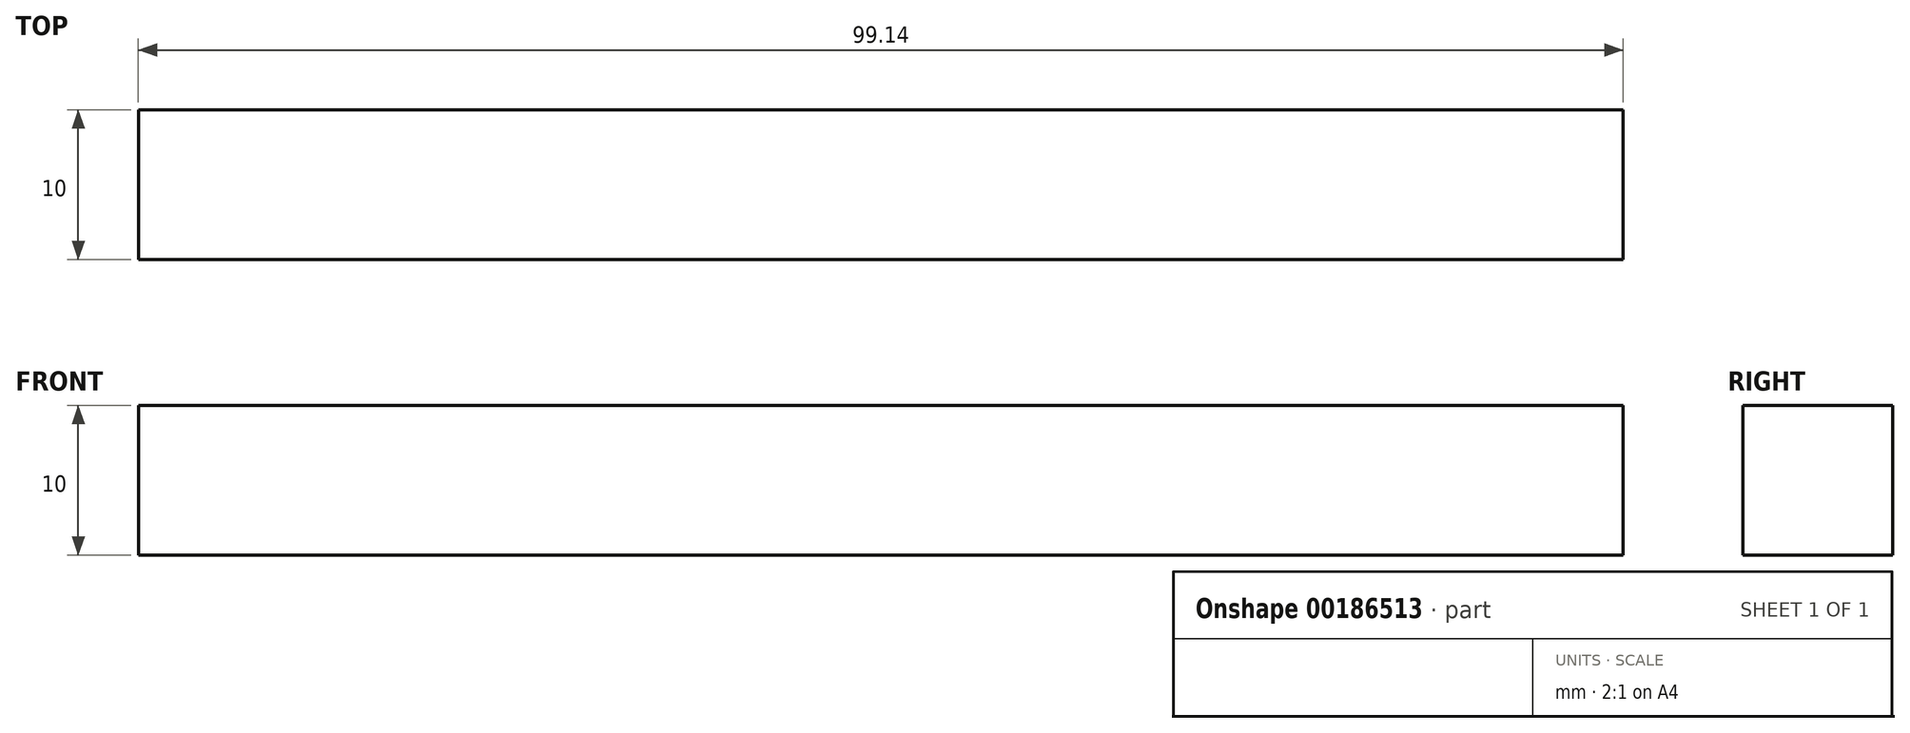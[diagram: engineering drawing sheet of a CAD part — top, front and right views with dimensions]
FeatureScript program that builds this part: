
annotation { "Feature Type Name" : "Feature", "Feature Type Description" : "" }
export const myFeature = defineFeature(function(context is Context, id is Id, definition is map)
    precondition{}
    {
        {
            var Q0;
            Q0=qCreatedBy(makeId("Front.planeOp"),FACE);
            var sketch = newSketch(context, id + "F0", { "sketchPlane" : qUnion([Q0])});
            skLineSegment(sketch, "E0.bottom", {"start": v(-42.53, -4.81) * mm, "end": v(56.6, -4.81) * mm});
            skLineSegment(sketch, "E0.top", {"start": v(-42.53, -14.81) * mm, "end": v(56.6, -14.81) * mm});
            skLineSegment(sketch, "E0.left", {"start": v(-42.53, -4.81) * mm, "end": v(-42.53, -14.81) * mm});
            skLineSegment(sketch, "E0.right", {"start": v(56.6, -4.81) * mm, "end": v(56.6, -14.81) * mm});
            skSolve(sketch);
        }
        {
            var Q0;
            Q0=makeQuery(id+"F0.imprint","IMPRINT",FACE,{"disambiguationData":[TD([[makeQuery(id+"F0.imprint","IMPRINT",EDGE,{"derivedFrom":sQuery(id+"F0.wireOp",EDGE,"E0.bottom")}),-1.0]])]});
            extrude(context, id + "F1", {"entities" : qUnion([Q0]), "depth" : 10 * mm});
        }
    });
